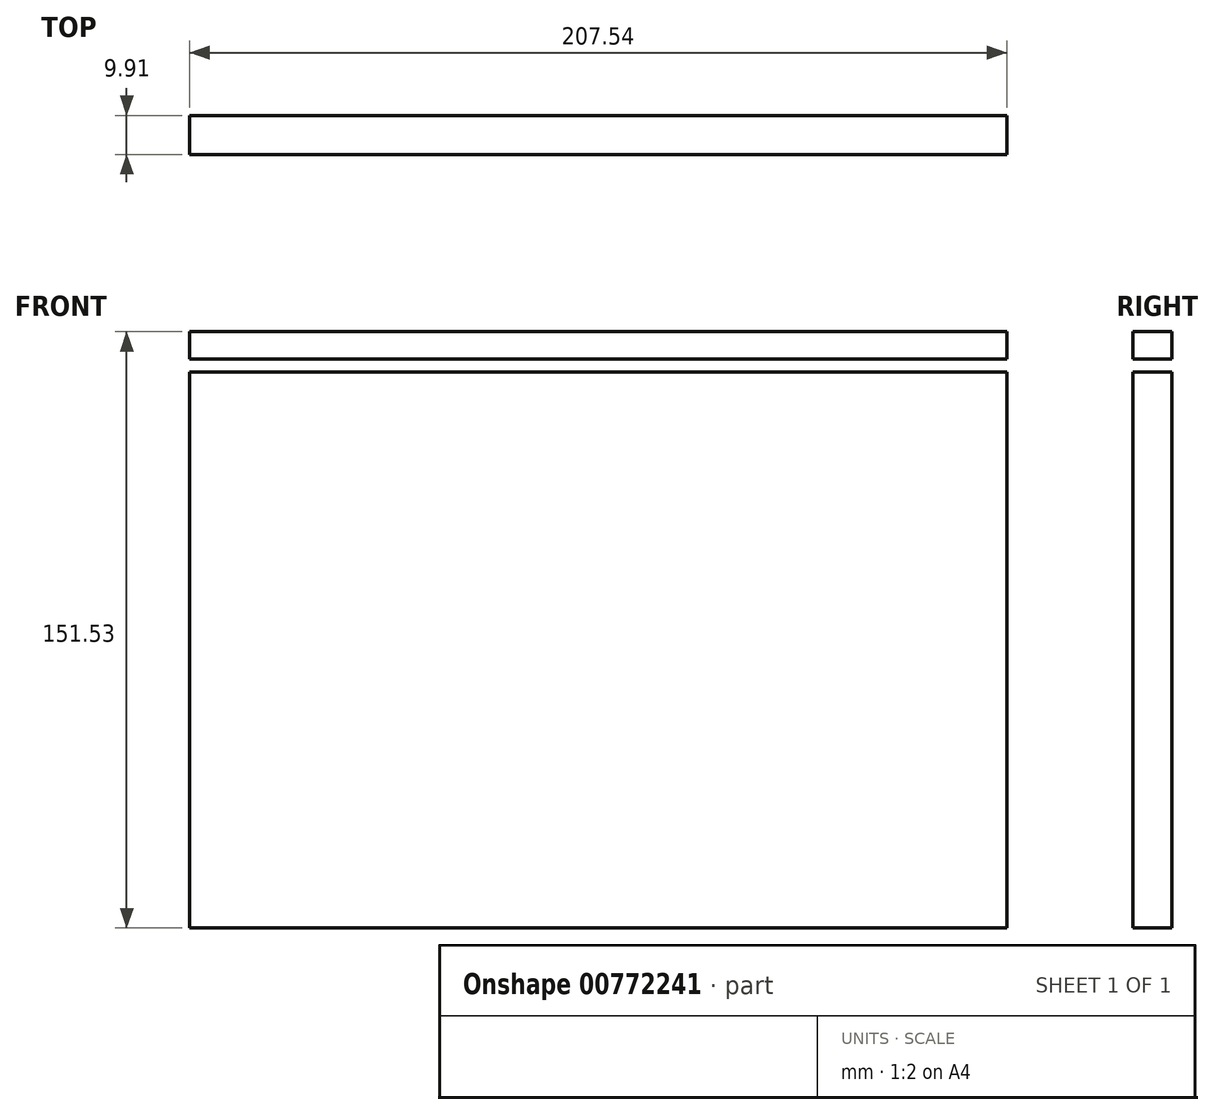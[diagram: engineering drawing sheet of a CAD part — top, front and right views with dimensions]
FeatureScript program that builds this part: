
annotation { "Feature Type Name" : "Feature", "Feature Type Description" : "" }
export const myFeature = defineFeature(function(context is Context, id is Id, definition is map)
    precondition{}
    {
        {
            var Q0;
            Q0=qCreatedBy(makeId("Front.planeOp"),FACE);
            var sketch = newSketch(context, id + "F0", { "sketchPlane" : qUnion([Q0])});
            skLineSegment(sketch, "E0", {"start": v(-118.4, 66.6) * mm, "end": v(118.4, 66.6) * mm});
            skLineSegment(sketch, "E1", {"start": v(118.4, 66.6) * mm, "end": v(118.4, 63.23) * mm});
            skLineSegment(sketch, "E2", {"start": v(118.4, 63.23) * mm, "end": v(-118.4, 63.23) * mm});
            skLineSegment(sketch, "E3", {"start": v(-118.4, 63.23) * mm, "end": v(-118.4, 66.6) * mm});
            skLineSegment(sketch, "E4", {"start": v(-118.4, 63.23) * mm, "end": v(-118.4, 63.23) * mm});
            skLineSegment(sketch, "E5", {"start": v(-100.82, 73.56) * mm, "end": v(-100.82, -77.97) * mm});
            skLineSegment(sketch, "E6", {"start": v(-100.82, -77.97) * mm, "end": v(106.72, -77.97) * mm});
            skLineSegment(sketch, "E7", {"start": v(106.72, -77.97) * mm, "end": v(106.72, 73.56) * mm});
            skLineSegment(sketch, "E8", {"start": v(106.72, 73.56) * mm, "end": v(-100.82, 73.56) * mm});
            skSolve(sketch);
        }
        {
            var Q0;
            {var subQ5=sQuery(id+"F0.wireOp",EDGE,"E6");Q0=makeQuery(id+"F0.imprint","IMPRINT",FACE,{"disambiguationData":[TD([[makeQuery(id+"F0.imprint","IMPRINT",EDGE,{"derivedFrom":subQ5}),1.0]])]});}
            var Q1;
            {var subQ5=sQuery(id+"F0.wireOp",EDGE,"E8");Q1=makeQuery(id+"F0.imprint","IMPRINT",FACE,{"disambiguationData":[TD([[makeQuery(id+"F0.imprint","IMPRINT",EDGE,{"derivedFrom":subQ5}),1.0]])]});}
            extrude(context, id + "F1", {"entities" : qUnion([Q0, Q1]), "depth" : 9.9 * mm, "offsetDistance" : 25.4 * mm});
        }
    });
